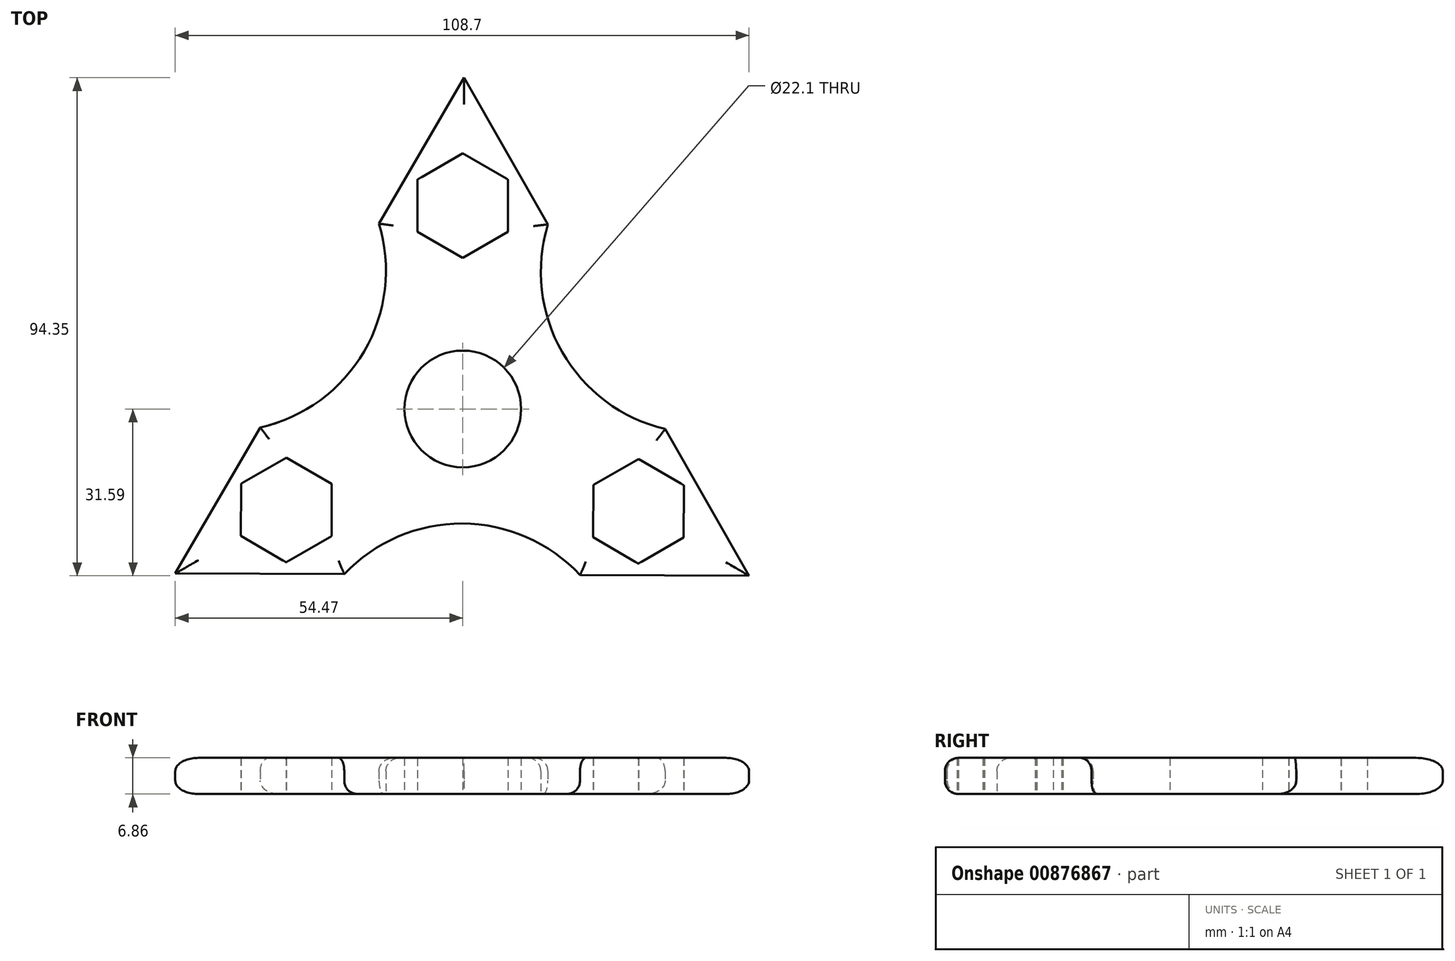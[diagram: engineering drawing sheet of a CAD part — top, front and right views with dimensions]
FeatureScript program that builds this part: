
annotation { "Feature Type Name" : "Feature", "Feature Type Description" : "" }
export const myFeature = defineFeature(function(context is Context, id is Id, definition is map)
    precondition{}
    {
        {
            var Q0;
            Q0=qCreatedBy(makeId("Top.planeOp"),FACE);
            var sketch = newSketch(context, id + "F0", { "sketchPlane" : qUnion([Q0])});
            skCircle(sketch, "E0.cCircle", {"center": v(0, 0) * mm, "radius": 31.38 * mm, "construction": true});
            skLineSegment(sketch, "E0.0", {"start": v(54.23, -31.6) * mm, "end": v(-54.47, -31.17) * mm});
            skLineSegment(sketch, "E0.1", {"start": v(-54.47, -31.17) * mm, "end": v(0.25, 62.76) * mm});
            skLineSegment(sketch, "E0.2", {"start": v(0.25, 62.76) * mm, "end": v(54.23, -31.6) * mm});
            skPoint(sketch, "E0.0.midPoint", {"position": v(-0.12, -31.38) * mm});
            skCircle(sketch, "E1", {"center": v(0, 0) * mm, "radius": 38.51 * mm, "construction": true});
            skCircle(sketch, "E2", {"center": v(0, 0) * mm, "radius": 21.47 * mm, "construction": true});
            skLineSegment(sketch, "E3", {"start": v(-54.47, -31.17) * mm, "end": v(27.24, 15.58) * mm, "construction": true});
            skLineSegment(sketch, "E4", {"start": v(54.23, -31.6) * mm, "end": v(-27.11, 15.8) * mm, "construction": true});
            skArc(sketch, "E5", {"start": v(16.15, 34.97) * mm, "mid": v(18.83, 10.77) * mm, "end": v(38.33, -3.8) * mm});
            skArc(sketch, "E6", {"start": v(-38.35, -3.5) * mm, "mid": v(-18.7, 10.9) * mm, "end": v(-15.87, 35.1) * mm});
            skArc(sketch, "E7", {"start": v(22.2, -31.47) * mm, "mid": v(-0.08, -21.71) * mm, "end": v(-22.45, -31.3) * mm});
            skLineSegment(sketch, "E8", {"start": v(-15.87, 35.1) * mm, "end": v(-38.35, -3.5) * mm});
            skCircle(sketch, "E9", {"center": v(0, 0) * mm, "radius": 11.05 * mm});
            skCircle(sketch, "E10.cCircle", {"center": v(-33.43, -19.13) * mm, "radius": 8.58 * mm, "construction": true});
            skLineSegment(sketch, "E10.0", {"start": v(-33.4, -9.22) * mm, "end": v(-24.83, -14.2) * mm});
            skLineSegment(sketch, "E10.1", {"start": v(-24.83, -14.2) * mm, "end": v(-24.87, -24.11) * mm});
            skLineSegment(sketch, "E10.2", {"start": v(-24.87, -24.11) * mm, "end": v(-33.47, -29.03) * mm});
            skLineSegment(sketch, "E10.3", {"start": v(-33.47, -29.03) * mm, "end": v(-42.03, -24.05) * mm});
            skLineSegment(sketch, "E10.4", {"start": v(-42.03, -24.05) * mm, "end": v(-41.99, -14.14) * mm});
            skLineSegment(sketch, "E10.5", {"start": v(-41.99, -14.14) * mm, "end": v(-33.4, -9.22) * mm});
            skPoint(sketch, "E10.0.midPoint", {"position": v(-29.11, -11.71) * mm});
            skCircle(sketch, "E11.cCircle", {"center": v(33.28, -19.39) * mm, "radius": 8.58 * mm, "construction": true});
            skLineSegment(sketch, "E11.0", {"start": v(24.72, -14.4) * mm, "end": v(33.32, -9.48) * mm});
            skLineSegment(sketch, "E11.1", {"start": v(33.32, -9.48) * mm, "end": v(41.88, -14.47) * mm});
            skLineSegment(sketch, "E11.2", {"start": v(41.88, -14.47) * mm, "end": v(41.84, -24.37) * mm});
            skLineSegment(sketch, "E11.3", {"start": v(41.84, -24.37) * mm, "end": v(33.24, -29.3) * mm});
            skLineSegment(sketch, "E11.4", {"start": v(33.24, -29.3) * mm, "end": v(24.68, -24.3) * mm});
            skLineSegment(sketch, "E11.5", {"start": v(24.68, -24.3) * mm, "end": v(24.72, -14.4) * mm});
            skPoint(sketch, "E11.0.midPoint", {"position": v(29.02, -11.94) * mm});
            skCircle(sketch, "E12.cCircle", {"center": v(0, 38.51) * mm, "radius": 8.58 * mm, "construction": true});
            skLineSegment(sketch, "E12.0", {"start": v(-8.57, 43.48) * mm, "end": v(0.01, 48.42) * mm});
            skLineSegment(sketch, "E12.1", {"start": v(0.01, 48.42) * mm, "end": v(8.58, 43.46) * mm});
            skLineSegment(sketch, "E12.2", {"start": v(8.58, 43.46) * mm, "end": v(8.57, 33.55) * mm});
            skLineSegment(sketch, "E12.3", {"start": v(8.57, 33.55) * mm, "end": v(-0.01, 28.6) * mm});
            skLineSegment(sketch, "E12.4", {"start": v(-0.01, 28.6) * mm, "end": v(-8.58, 33.57) * mm});
            skLineSegment(sketch, "E12.5", {"start": v(-8.58, 33.57) * mm, "end": v(-8.57, 43.48) * mm});
            skPoint(sketch, "E12.0.midPoint", {"position": v(-4.28, 45.95) * mm});
            skSolve(sketch);
        }
        {
            var Q0;
            Q0 = qSketchRegion(id + "F0", true);
            extrude(context, id + "F1", {"entities" : qUnion([Q0]), "depth" : 6.86 * mm, "offsetDistance" : 25.4 * mm});
        }
        {
            var Q0;
            Q0=makeQuery(id+"F0.imprint","IMPRINT",FACE,{"disambiguationData":[TD([[makeQuery(id+"F0.imprint","IMPRINT",EDGE,{"derivedFrom":sQuery(id+"F0.wireOp",EDGE,"E6")}),1.0]])]});
            extrude(context, id + "F2", {"entities" : qUnion([Q0]), "operationType" : NewBodyOperationType.REMOVE, "depth" : 47 * mm, "offsetDistance" : 25.4 * mm});
        }
        {
            var Q0;
            {var subQ0=sQuery(id+"F0.wireOp",EDGE,"E7");Q0=makeQuery(id+"F0.imprint","IMPRINT",FACE,{"disambiguationData":[TD([[makeQuery(id+"F0.imprint","IMPRINT",EDGE,{"derivedFrom":subQ0}),1.0]])]});}
            extrude(context, id + "F3", {"entities" : qUnion([Q0]), "operationType" : NewBodyOperationType.REMOVE, "depth" : 37.6 * mm, "offsetDistance" : 25.4 * mm});
        }
        {
            var Q0;
            {var subQ0=sQuery(id+"F0.wireOp",EDGE,"E5");Q0=makeQuery(id+"F0.imprint","IMPRINT",FACE,{"disambiguationData":[TD([[makeQuery(id+"F0.imprint","IMPRINT",EDGE,{"derivedFrom":subQ0}),1.0]])]});}
            extrude(context, id + "F4", {"entities" : qUnion([Q0]), "operationType" : NewBodyOperationType.REMOVE, "depth" : 42.42 * mm, "offsetDistance" : 25.4 * mm});
        }
        {
            var Q0;
            Q0=makeQuery(id+"F0.imprint","IMPRINT",FACE,{"disambiguationData":[TD([[makeQuery(id+"F0.imprint","IMPRINT",EDGE,{"derivedFrom":sQuery(id+"F0.wireOp",EDGE,"E9")}),1.0]])]});
            extrude(context, id + "F5", {"entities" : qUnion([Q0]), "operationType" : NewBodyOperationType.REMOVE, "depth" : 29.72 * mm, "offsetDistance" : 25.4 * mm});
        }
        {
            var Q0;
            Q0=makeQuery(id+"F0.imprint","IMPRINT",FACE,{"disambiguationData":[TD([[makeQuery(id+"F0.imprint","IMPRINT",EDGE,{"derivedFrom":sQuery(id+"F0.wireOp",EDGE,"E9")}),1.0]])]});
            extrude(context, id + "F6", {"entities" : qUnion([Q0]), "operationType" : NewBodyOperationType.REMOVE, "depth" : 25.4 * mm, "offsetDistance" : 25.4 * mm});
        }
        {
            var Q0;
            {var subQ0=sQuery(id+"F0.wireOp",EDGE,"E8");var subQ1=sQuery(id+"F0.wireOp",EDGE,"E0.2");var subQ2=sQuery(id+"F0.wireOp",EDGE,"E0.1");Q0=makeQuery(id+"F4.boolean.opBoolean","SPLIT",EDGE,{"disambiguationData":[TD([makeQuery(id+"F1.opExtrude","SWEPT_FACE",FACE,{"disambiguationData":[OSD([subQ2,subQ0])]})])],"derivedFrom":makeQuery(id+"F1.opExtrude","CAP_EDGE",EDGE,{"disambiguationData":[OSD([subQ1])],"isStart":true})});}
            var Q1;
            Q1=makeQuery(id+"F4.boolean.opBoolean","COPY",EDGE,{"derivedFrom":makeQuery(id+"F4.opExtrude","CAP_EDGE",EDGE,{"disambiguationData":[OSD([sQuery(id+"F0.wireOp",EDGE,"E5")])],"isStart":true})});
            var Q2;
            {var subQ0=sQuery(id+"F0.wireOp",EDGE,"E0.0");var subQ1=sQuery(id+"F0.wireOp",EDGE,"E0.2");Q2=makeQuery(id+"F4.boolean.opBoolean","SPLIT",EDGE,{"disambiguationData":[TD([makeQuery(id+"F1.opExtrude","SWEPT_FACE",FACE,{"disambiguationData":[OSD([subQ0])]})])],"derivedFrom":makeQuery(id+"F1.opExtrude","CAP_EDGE",EDGE,{"disambiguationData":[OSD([subQ1])],"isStart":true})});}
            var Q3;
            {var subQ0=sQuery(id+"F0.wireOp",EDGE,"E0.0");var subQ1=sQuery(id+"F0.wireOp",EDGE,"E0.2");Q3=makeQuery(id+"F3.boolean.opBoolean","SPLIT",EDGE,{"disambiguationData":[TD([makeQuery(id+"F1.opExtrude","SWEPT_FACE",FACE,{"disambiguationData":[OSD([subQ1])]})])],"derivedFrom":makeQuery(id+"F1.opExtrude","CAP_EDGE",EDGE,{"disambiguationData":[OSD([subQ0])],"isStart":true})});}
            var Q4;
            Q4=makeQuery(id+"F3.boolean.opBoolean","COPY",EDGE,{"derivedFrom":makeQuery(id+"F3.opExtrude","CAP_EDGE",EDGE,{"disambiguationData":[OSD([sQuery(id+"F0.wireOp",EDGE,"E7")])],"isStart":true})});
            var Q5;
            {var subQ0=sQuery(id+"F0.wireOp",EDGE,"E0.0");var subQ1=sQuery(id+"F0.wireOp",EDGE,"E8");var subQ2=sQuery(id+"F0.wireOp",EDGE,"E0.1");Q5=makeQuery(id+"F2.boolean.opBoolean","SPLIT",EDGE,{"disambiguationData":[TD([makeQuery(id+"F1.opExtrude","SWEPT_FACE",FACE,{"disambiguationData":[OSD([subQ0])]})])],"derivedFrom":makeQuery(id+"F1.opExtrude","CAP_EDGE",EDGE,{"disambiguationData":[OSD([subQ2,subQ1])],"isStart":true})});}
            var Q6;
            {var subQ0=sQuery(id+"F0.wireOp",EDGE,"E0.0");var subQ1=sQuery(id+"F0.wireOp",EDGE,"E8");var subQ2=sQuery(id+"F0.wireOp",EDGE,"E0.1");Q6=makeQuery(id+"F3.boolean.opBoolean","SPLIT",EDGE,{"disambiguationData":[TD([makeQuery(id+"F1.opExtrude","SWEPT_FACE",FACE,{"disambiguationData":[OSD([subQ2,subQ1])]})])],"derivedFrom":makeQuery(id+"F1.opExtrude","CAP_EDGE",EDGE,{"disambiguationData":[OSD([subQ0])],"isStart":true})});}
            var Q7;
            Q7=makeQuery(id+"F2.boolean.opBoolean","COPY",EDGE,{"derivedFrom":makeQuery(id+"F2.opExtrude","CAP_EDGE",EDGE,{"disambiguationData":[OSD([sQuery(id+"F0.wireOp",EDGE,"E6")])],"isStart":true})});
            var Q8;
            {var subQ0=sQuery(id+"F0.wireOp",EDGE,"E8");var subQ1=sQuery(id+"F0.wireOp",EDGE,"E0.2");var subQ2=sQuery(id+"F0.wireOp",EDGE,"E0.1");Q8=makeQuery(id+"F2.boolean.opBoolean","SPLIT",EDGE,{"disambiguationData":[TD([makeQuery(id+"F1.opExtrude","SWEPT_FACE",FACE,{"disambiguationData":[OSD([subQ1])]})])],"derivedFrom":makeQuery(id+"F1.opExtrude","CAP_EDGE",EDGE,{"disambiguationData":[OSD([subQ2,subQ0])],"isStart":true})});}
            var Q9;
            {var subQ0=sQuery(id+"F0.wireOp",EDGE,"E8");var subQ1=sQuery(id+"F0.wireOp",EDGE,"E0.2");var subQ2=sQuery(id+"F0.wireOp",EDGE,"E0.1");Q9=makeQuery(id+"F2.boolean.opBoolean","SPLIT",EDGE,{"disambiguationData":[TD([makeQuery(id+"F1.opExtrude","SWEPT_FACE",FACE,{"disambiguationData":[OSD([subQ1])]})])],"derivedFrom":makeQuery(id+"F1.opExtrude","CAP_EDGE",EDGE,{"disambiguationData":[OSD([subQ2,subQ0])],"isStart":false})});}
            var Q10;
            Q10=makeQuery(id+"F2.boolean.opBoolean","INTERSECT",EDGE,{"derivedFrom":[makeQuery(id+"F1.opExtrude","CAP_FACE",FACE,{"disambiguationData":[OSD([sQuery(id+"F0.wireOp",EDGE,"E0.0"),sQuery(id+"F0.wireOp",EDGE,"E0.1"),sQuery(id+"F0.wireOp",EDGE,"E0.2"),sQuery(id+"F0.wireOp",EDGE,"E8"),sQuery(id+"F0.wireOp",EDGE,"E9"),sQuery(id+"F0.wireOp",EDGE,"E10.0"),sQuery(id+"F0.wireOp",EDGE,"E10.1"),sQuery(id+"F0.wireOp",EDGE,"E10.2"),sQuery(id+"F0.wireOp",EDGE,"E10.3"),sQuery(id+"F0.wireOp",EDGE,"E10.4"),sQuery(id+"F0.wireOp",EDGE,"E10.5"),sQuery(id+"F0.wireOp",EDGE,"E11.0"),sQuery(id+"F0.wireOp",EDGE,"E11.1"),sQuery(id+"F0.wireOp",EDGE,"E11.2"),sQuery(id+"F0.wireOp",EDGE,"E11.3"),sQuery(id+"F0.wireOp",EDGE,"E11.4"),sQuery(id+"F0.wireOp",EDGE,"E11.5"),sQuery(id+"F0.wireOp",EDGE,"E12.0"),sQuery(id+"F0.wireOp",EDGE,"E12.1"),sQuery(id+"F0.wireOp",EDGE,"E12.2"),sQuery(id+"F0.wireOp",EDGE,"E12.3"),sQuery(id+"F0.wireOp",EDGE,"E12.4"),sQuery(id+"F0.wireOp",EDGE,"E12.5")])],"isStart":false}),makeQuery(id+"F2.opExtrude","SWEPT_FACE",FACE,{"disambiguationData":[OSD([sQuery(id+"F0.wireOp",EDGE,"E6")])]})]});
            var Q11;
            {var subQ0=sQuery(id+"F0.wireOp",EDGE,"E0.0");var subQ1=sQuery(id+"F0.wireOp",EDGE,"E8");var subQ2=sQuery(id+"F0.wireOp",EDGE,"E0.1");Q11=makeQuery(id+"F2.boolean.opBoolean","SPLIT",EDGE,{"disambiguationData":[TD([makeQuery(id+"F1.opExtrude","SWEPT_FACE",FACE,{"disambiguationData":[OSD([subQ0])]})])],"derivedFrom":makeQuery(id+"F1.opExtrude","CAP_EDGE",EDGE,{"disambiguationData":[OSD([subQ2,subQ1])],"isStart":false})});}
            var Q12;
            {var subQ0=sQuery(id+"F0.wireOp",EDGE,"E0.0");var subQ1=sQuery(id+"F0.wireOp",EDGE,"E8");var subQ2=sQuery(id+"F0.wireOp",EDGE,"E0.1");Q12=makeQuery(id+"F3.boolean.opBoolean","SPLIT",EDGE,{"disambiguationData":[TD([makeQuery(id+"F1.opExtrude","SWEPT_FACE",FACE,{"disambiguationData":[OSD([subQ2,subQ1])]})])],"derivedFrom":makeQuery(id+"F1.opExtrude","CAP_EDGE",EDGE,{"disambiguationData":[OSD([subQ0])],"isStart":false})});}
            var Q13;
            {var subQ0=sQuery(id+"F0.wireOp",EDGE,"E0.0");var subQ1=sQuery(id+"F0.wireOp",EDGE,"E0.2");Q13=makeQuery(id+"F3.boolean.opBoolean","SPLIT",EDGE,{"disambiguationData":[TD([makeQuery(id+"F1.opExtrude","SWEPT_FACE",FACE,{"disambiguationData":[OSD([subQ1])]})])],"derivedFrom":makeQuery(id+"F1.opExtrude","CAP_EDGE",EDGE,{"disambiguationData":[OSD([subQ0])],"isStart":false})});}
            var Q14;
            Q14=makeQuery(id+"F3.boolean.opBoolean","INTERSECT",EDGE,{"derivedFrom":[makeQuery(id+"F1.opExtrude","CAP_FACE",FACE,{"disambiguationData":[OSD([sQuery(id+"F0.wireOp",EDGE,"E0.0"),sQuery(id+"F0.wireOp",EDGE,"E0.1"),sQuery(id+"F0.wireOp",EDGE,"E0.2"),sQuery(id+"F0.wireOp",EDGE,"E8"),sQuery(id+"F0.wireOp",EDGE,"E9"),sQuery(id+"F0.wireOp",EDGE,"E10.0"),sQuery(id+"F0.wireOp",EDGE,"E10.1"),sQuery(id+"F0.wireOp",EDGE,"E10.2"),sQuery(id+"F0.wireOp",EDGE,"E10.3"),sQuery(id+"F0.wireOp",EDGE,"E10.4"),sQuery(id+"F0.wireOp",EDGE,"E10.5"),sQuery(id+"F0.wireOp",EDGE,"E11.0"),sQuery(id+"F0.wireOp",EDGE,"E11.1"),sQuery(id+"F0.wireOp",EDGE,"E11.2"),sQuery(id+"F0.wireOp",EDGE,"E11.3"),sQuery(id+"F0.wireOp",EDGE,"E11.4"),sQuery(id+"F0.wireOp",EDGE,"E11.5"),sQuery(id+"F0.wireOp",EDGE,"E12.0"),sQuery(id+"F0.wireOp",EDGE,"E12.1"),sQuery(id+"F0.wireOp",EDGE,"E12.2"),sQuery(id+"F0.wireOp",EDGE,"E12.3"),sQuery(id+"F0.wireOp",EDGE,"E12.4"),sQuery(id+"F0.wireOp",EDGE,"E12.5")])],"isStart":false}),makeQuery(id+"F3.opExtrude","SWEPT_FACE",FACE,{"disambiguationData":[OSD([sQuery(id+"F0.wireOp",EDGE,"E7")])]})]});
            var Q15;
            Q15=makeQuery(id+"F4.boolean.opBoolean","INTERSECT",EDGE,{"derivedFrom":[makeQuery(id+"F1.opExtrude","CAP_FACE",FACE,{"disambiguationData":[OSD([sQuery(id+"F0.wireOp",EDGE,"E0.0"),sQuery(id+"F0.wireOp",EDGE,"E0.1"),sQuery(id+"F0.wireOp",EDGE,"E0.2"),sQuery(id+"F0.wireOp",EDGE,"E8"),sQuery(id+"F0.wireOp",EDGE,"E9"),sQuery(id+"F0.wireOp",EDGE,"E10.0"),sQuery(id+"F0.wireOp",EDGE,"E10.1"),sQuery(id+"F0.wireOp",EDGE,"E10.2"),sQuery(id+"F0.wireOp",EDGE,"E10.3"),sQuery(id+"F0.wireOp",EDGE,"E10.4"),sQuery(id+"F0.wireOp",EDGE,"E10.5"),sQuery(id+"F0.wireOp",EDGE,"E11.0"),sQuery(id+"F0.wireOp",EDGE,"E11.1"),sQuery(id+"F0.wireOp",EDGE,"E11.2"),sQuery(id+"F0.wireOp",EDGE,"E11.3"),sQuery(id+"F0.wireOp",EDGE,"E11.4"),sQuery(id+"F0.wireOp",EDGE,"E11.5"),sQuery(id+"F0.wireOp",EDGE,"E12.0"),sQuery(id+"F0.wireOp",EDGE,"E12.1"),sQuery(id+"F0.wireOp",EDGE,"E12.2"),sQuery(id+"F0.wireOp",EDGE,"E12.3"),sQuery(id+"F0.wireOp",EDGE,"E12.4"),sQuery(id+"F0.wireOp",EDGE,"E12.5")])],"isStart":false}),makeQuery(id+"F4.opExtrude","SWEPT_FACE",FACE,{"disambiguationData":[OSD([sQuery(id+"F0.wireOp",EDGE,"E5")])]})]});
            var Q16;
            {var subQ0=sQuery(id+"F0.wireOp",EDGE,"E0.0");var subQ1=sQuery(id+"F0.wireOp",EDGE,"E0.2");Q16=makeQuery(id+"F4.boolean.opBoolean","SPLIT",EDGE,{"disambiguationData":[TD([makeQuery(id+"F1.opExtrude","SWEPT_FACE",FACE,{"disambiguationData":[OSD([subQ0])]})])],"derivedFrom":makeQuery(id+"F1.opExtrude","CAP_EDGE",EDGE,{"disambiguationData":[OSD([subQ1])],"isStart":false})});}
            var Q17;
            {var subQ0=sQuery(id+"F0.wireOp",EDGE,"E8");var subQ1=sQuery(id+"F0.wireOp",EDGE,"E0.2");var subQ2=sQuery(id+"F0.wireOp",EDGE,"E0.1");Q17=makeQuery(id+"F4.boolean.opBoolean","SPLIT",EDGE,{"disambiguationData":[TD([makeQuery(id+"F1.opExtrude","SWEPT_FACE",FACE,{"disambiguationData":[OSD([subQ2,subQ0])]})])],"derivedFrom":makeQuery(id+"F1.opExtrude","CAP_EDGE",EDGE,{"disambiguationData":[OSD([subQ1])],"isStart":false})});}
            fillet(context, id + "F7", {"entities" : qUnion([Q0, Q1, Q2, Q3, Q4, Q5, Q6, Q7, Q8, Q9, Q10, Q11, Q12, Q13, Q14, Q15, Q16, Q17]), "radius" : 2.54 * mm, "tangentPropagation" : true, "allowEdgeOverflow" : false});
        }
    });
